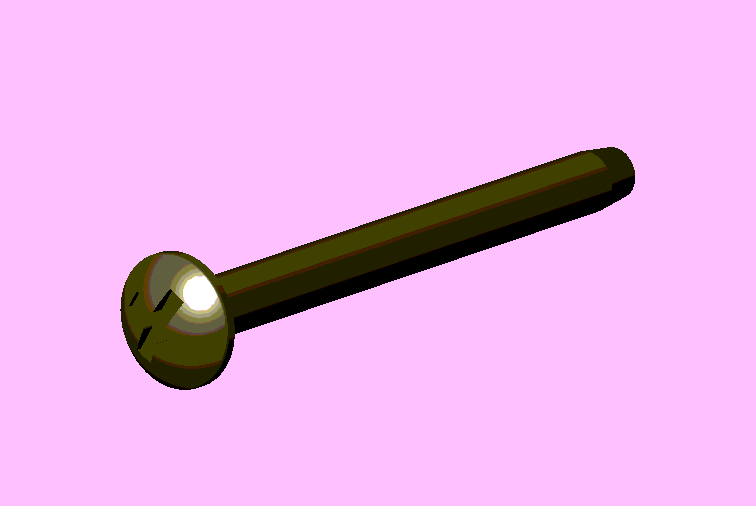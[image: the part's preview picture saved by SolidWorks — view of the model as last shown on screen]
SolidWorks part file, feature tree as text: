
SOLIDWORKS PART (.sldprt)
format: sldprt  version: not decoded by parser v0  size: 139,264 bytes
history: native  units: mm
features: plane x4, sketch x4, fillet x2, material x1, revolve x1, extrude x1, chamfer x1, cut_extrude x1 (+8 scaffold rows collapsed)
feature tree (23):
  scaffold x8  (default folders/planes/origin — collapsed)
  material  "Matériau <non spécifié>"
  plane  "Plane1"
  plane  "Plane2"
  plane  "Plane3"
  sketch  "Esquisse1"  dims[D1=9.0mm D2=32.0mm D3=3.0mm]
  revolve  "Base-Révolution"  Angle=360deg
  sketch  "Esquisse2"
  extrude  "Boss.-Extru.1"  Depth=0.5mm
  fillet  "Congé1"  Radius=0.25mm
  sketch  "Esquisse3"  dims[D1=3.0mm]
  fillet  "Boss.-Extru.2"  Radius=32mm
  chamfer  "Chanfrein1"  Distance=2mm
  plane  "Plan1"  Offset=3mm
  sketch  "Esquisse4"  dims[D3=1.5mm D1=1.0mm D2=2.0mm]
  cut_extrude  "Enlèv. mat.-Extru.2"  Depth=1.75mm
decode coverage: 9 of 10 modeling features carry decoded parameters
note: suppression state not decoded; provenance and decode notes live in map.json
